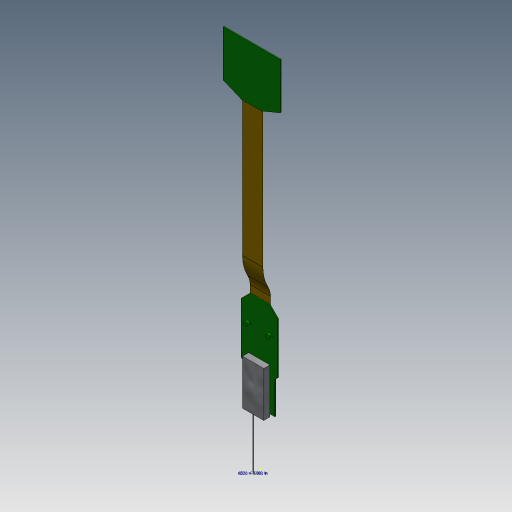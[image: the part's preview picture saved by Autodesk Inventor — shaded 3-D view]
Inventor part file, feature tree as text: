
AUTODESK INVENTOR PART (.ipt)
format: ipt  version: 2023.4 (Build 274418000, 418)  size: 1,069,056 bytes
history: native  units: in
note: dims shown in document units (in); Inventor stores cm internally (conversion verified against a paired STEP export)
features: extrude x6, plane x3, other x3, projected_geometry x3, sketch x2
ambient origin geometry x8: Origin, YZ Plane, XZ Plane, XY Plane, X Axis, Y Axis, Z Axis, Center Point
bodies: Body1 (feature_tree)
feature tree (17):
  sketch  "Sketch1"  dims[d175=0.3937in d243=0.73in]
  plane  "Work Plane4"
  extrude  "Extrusion4"  Depth=0.73in
  sketch  "Sketch3"  dims[d244=0.365in d245=0.28in d246=0.155in d247=0.46in d252=0.008in d253=0.0in d263=1.335in d264=0.153in d265=0.442in d266=0.221in d267=0.417in d268=0.357in d269=0.357in d277=0.007in d283=0.165in d284=0.02in d285=0.35in d286=0.048in d287=0.0in d288=0.0028in d289=0.0028in d290=0.3937in d291=0.0in d292=0.1685in d294=0.0842in d295=0.033in d296=0.02in d297=0.0in d298=0.0295in d299=0.008in d300=0.0in d301=1.725in d307=0.7734in d308=0.417in d312=0.1575in d313=0.0in d314=0.2in d318=0.06in d320=0.0014in d321=0.0014in]
  plane  "Work Plane1"
  plane  "Work Plane2"
  extrude  "Extrusion11"  Depth=0.28in
  extrude  "Extrusion8"  Depth=0.06in
  extrude  "Extrusion9"  Depth=0.06in
  extrude  "Extrusion10"  Depth=0.008in TaperAngle=0.0deg
  extrude  "Extrusion12"  Depth=1.335in
  other  "Work Point1"
  other  "Image3"
  other  "Image4"
  projected_geometry  "Projected Loop1"
  projected_geometry  "Projected Loop2"
  projected_geometry  "Projected Loop3"
